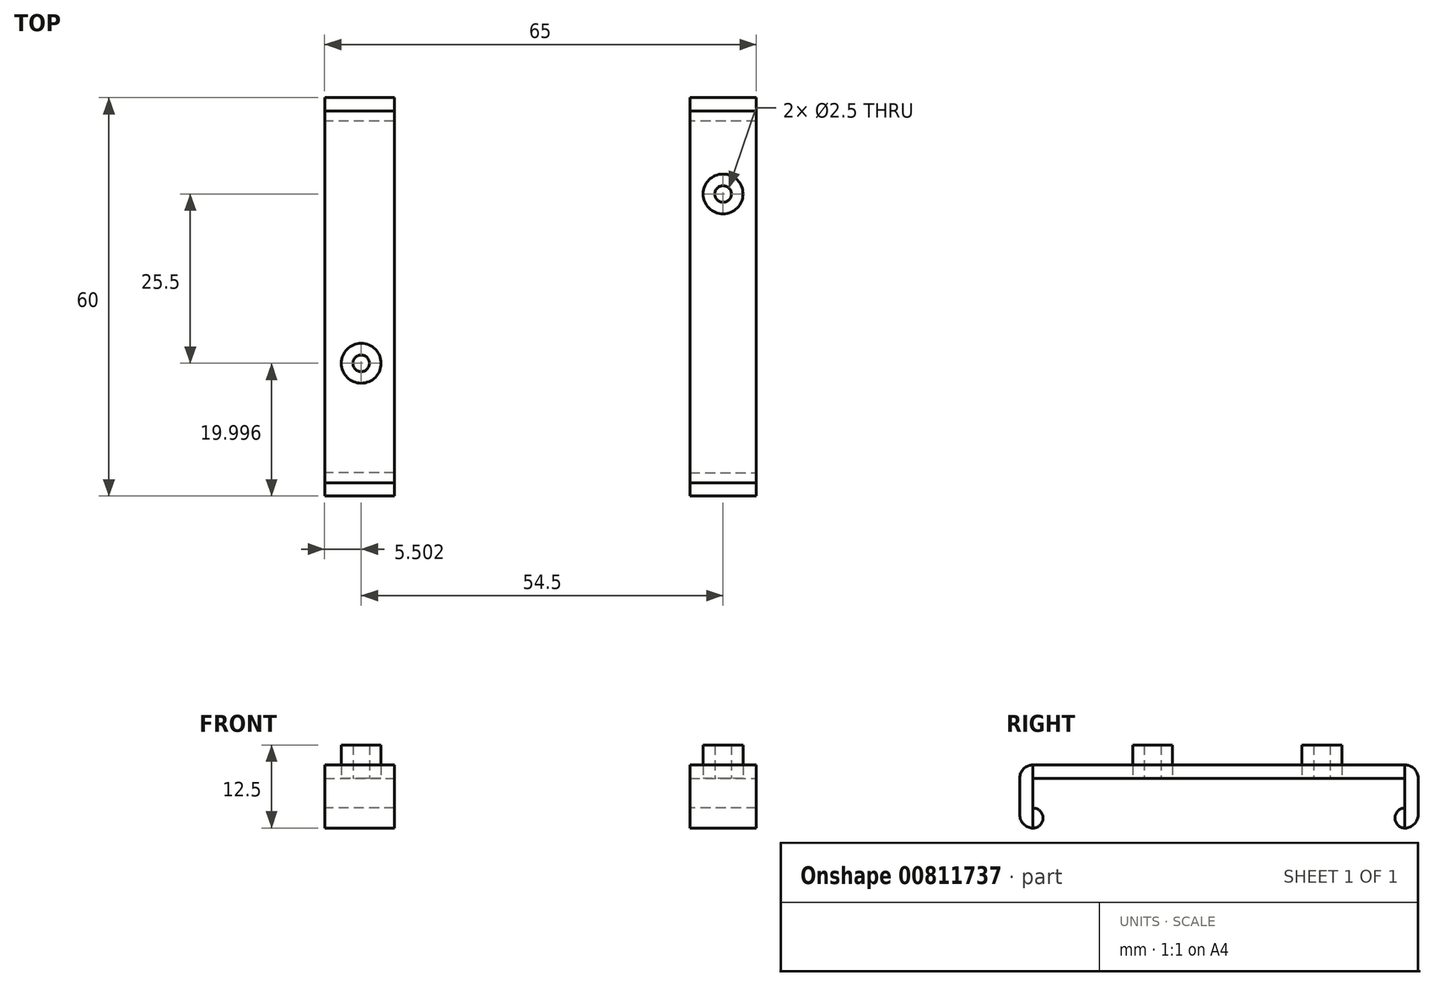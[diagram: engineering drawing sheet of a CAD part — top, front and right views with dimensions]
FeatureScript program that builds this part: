
annotation { "Feature Type Name" : "Feature", "Feature Type Description" : "" }
export const myFeature = defineFeature(function(context is Context, id is Id, definition is map)
    precondition{}
    {
        {
            var Q0;
            Q0=qCreatedBy(makeId("Top.planeOp"),FACE);
            var sketch = newSketch(context, id + "F0", { "sketchPlane" : qUnion([Q0])});
            skLineSegment(sketch, "E0.bottom", {"start": v(-22.77, 10.2) * mm, "end": v(62.23, 10.2) * mm, "construction": true});
            skLineSegment(sketch, "E0.top", {"start": v(-22.77, -45.8) * mm, "end": v(62.23, -45.8) * mm, "construction": true});
            skLineSegment(sketch, "E0.left", {"start": v(-22.77, 10.2) * mm, "end": v(-22.77, -45.8) * mm, "construction": true});
            skLineSegment(sketch, "E0.right", {"start": v(62.23, 10.2) * mm, "end": v(62.23, -45.8) * mm, "construction": true});
            skCircle(sketch, "E1", {"center": v(2.73, -27.8) * mm, "radius": 3 * mm});
            skCircle(sketch, "E2", {"center": v(2.73, -27.8) * mm, "radius": 1.25 * mm});
            skCircle(sketch, "E3", {"center": v(57.23, -2.3) * mm, "radius": 3 * mm});
            skCircle(sketch, "E4", {"center": v(57.23, -2.3) * mm, "radius": 1.25 * mm});
            skSolve(sketch);
        }
        {
            var Q0;
            Q0=makeQuery(id+"F0.imprint","IMPRINT",FACE,{"disambiguationData":[TD([[makeQuery(id+"F0.imprint","IMPRINT",EDGE,{"derivedFrom":sQuery(id+"F0.wireOp",EDGE,"E1")}),1.0]])]});
            var Q1;
            Q1=makeQuery(id+"F0.imprint","IMPRINT",FACE,{"disambiguationData":[TD([[makeQuery(id+"F0.imprint","IMPRINT",EDGE,{"derivedFrom":sQuery(id+"F0.wireOp",EDGE,"E3")}),1.0]])]});
            extrude(context, id + "F1", {"entities" : qUnion([Q0, Q1]), "depth" : 5 * mm, "offsetDistance" : 25 * mm});
        }
        {
            var Q0;
            Q0=qCreatedBy(makeId("Top.planeOp"),FACE);
            var sketch = newSketch(context, id + "F2", { "sketchPlane" : qUnion([Q0])});
            skLineSegment(sketch, "E5.bottom", {"start": v(-2.77, 10.2) * mm, "end": v(62.23, 10.2) * mm});
            skLineSegment(sketch, "E5.top", {"start": v(-2.77, -45.8) * mm, "end": v(62.23, -45.8) * mm});
            skLineSegment(sketch, "E5.left", {"start": v(-2.77, 10.2) * mm, "end": v(-2.77, -45.8) * mm});
            skLineSegment(sketch, "E5.right", {"start": v(62.23, 10.2) * mm, "end": v(62.23, -45.8) * mm});
            skLineSegment(sketch, "E6", {"start": v(7.73, 10.2) * mm, "end": v(7.73, -45.8) * mm});
            skLineSegment(sketch, "E7", {"start": v(52.23, 10.2) * mm, "end": v(52.23, -45.8) * mm});
            skSolve(sketch);
        }
        {
            var Q0;
            {var subQ0=sQuery(id+"F2.wireOp",EDGE,"E5.left");Q0=makeQuery(id+"F2.imprint","IMPRINT",FACE,{"disambiguationData":[TD([[makeQuery(id+"F2.imprint","IMPRINT",EDGE,{"derivedFrom":subQ0}),1.0]])]});}
            var Q1;
            {var subQ0=sQuery(id+"F2.wireOp",EDGE,"E5.right");Q1=makeQuery(id+"F2.imprint","IMPRINT",FACE,{"disambiguationData":[TD([[makeQuery(id+"F2.imprint","IMPRINT",EDGE,{"derivedFrom":subQ0}),-1.0]])]});}
            extrude(context, id + "F3", {"entities" : qUnion([Q0, Q1]), "depth" : 2 * mm, "offsetDistance" : 25 * mm});
        }
        {
            var Q0;
            Q0=makeQuery(id+"F3.opExtrude","SWEPT_FACE",FACE,{"disambiguationData":[OSD([sQuery(id+"F2.wireOp",EDGE,"E5.bottom")])]});
            var sketch = newSketch(context, id + "F4", { "sketchPlane" : qUnion([Q0])});
            skLineSegment(sketch, "E8.bottom", {"start": v(-62.23, 2) * mm, "end": v(-52.23, 2) * mm});
            skLineSegment(sketch, "E8.top", {"start": v(-62.23, -7.5) * mm, "end": v(-52.23, -7.5) * mm});
            skLineSegment(sketch, "E8.left", {"start": v(-62.23, 2) * mm, "end": v(-62.23, -7.5) * mm});
            skLineSegment(sketch, "E8.right", {"start": v(-52.23, 2) * mm, "end": v(-52.23, -7.5) * mm});
            skLineSegment(sketch, "E9", {"start": v(-62.23, -4.5) * mm, "end": v(-52.23, -4.5) * mm});
            skLineSegment(sketch, "E10.bottom", {"start": v(-7.73, 2) * mm, "end": v(2.77, 2) * mm});
            skLineSegment(sketch, "E10.top", {"start": v(-7.73, -7.5) * mm, "end": v(2.77, -7.5) * mm});
            skLineSegment(sketch, "E10.left", {"start": v(-7.73, 2) * mm, "end": v(-7.73, -7.5) * mm});
            skLineSegment(sketch, "E10.right", {"start": v(2.77, 2) * mm, "end": v(2.77, -7.5) * mm});
            skLineSegment(sketch, "E11", {"start": v(-7.73, -4.5) * mm, "end": v(2.77, -4.5) * mm});
            skSolve(sketch);
        }
        {
            var Q0;
            {var subQ0=sQuery(id+"F2.wireOp",EDGE,"E5.top");Q0=makeQuery(id+"F3.opExtrude","SWEPT_FACE",FACE,{"disambiguationData":[OSD([subQ0]),TDD([makeQuery(id+"F2.imprint","IMPRINT",EDGE,{"disambiguationData":[TD([[makeQuery(id+"F2.imprint","INTERSECT",VERTEX,{"derivedFrom":[subQ0,sQuery(id+"F2.wireOp",EDGE,"E5.left")]}),-1.0]])],"derivedFrom":subQ0})])]});}
            var sketch = newSketch(context, id + "F5", { "sketchPlane" : qUnion([Q0])});
            skLineSegment(sketch, "E12.bottom", {"start": v(-2.77, 2) * mm, "end": v(7.73, 2) * mm});
            skLineSegment(sketch, "E12.top", {"start": v(-2.77, -7.5) * mm, "end": v(7.73, -7.5) * mm});
            skLineSegment(sketch, "E12.left", {"start": v(-2.77, 2) * mm, "end": v(-2.77, -7.5) * mm});
            skLineSegment(sketch, "E12.right", {"start": v(7.73, 2) * mm, "end": v(7.73, -7.5) * mm});
            skLineSegment(sketch, "E13", {"start": v(-2.77, -4.5) * mm, "end": v(7.73, -4.5) * mm});
            skLineSegment(sketch, "E14.bottom", {"start": v(52.23, 2) * mm, "end": v(62.23, 2) * mm});
            skLineSegment(sketch, "E14.top", {"start": v(52.23, -7.5) * mm, "end": v(62.23, -7.5) * mm});
            skLineSegment(sketch, "E14.left", {"start": v(52.23, 2) * mm, "end": v(52.23, -7.5) * mm});
            skLineSegment(sketch, "E14.right", {"start": v(62.23, 2) * mm, "end": v(62.23, -7.5) * mm});
            skLineSegment(sketch, "E15", {"start": v(52.23, -4.5) * mm, "end": v(62.23, -4.5) * mm});
            skSolve(sketch);
        }
        {
            var Q0;
            {var subQ0=sQuery(id+"F4.wireOp",EDGE,"E10.bottom");Q0=makeQuery(id+"F4.imprint","IMPRINT",FACE,{"disambiguationData":[TD([[makeQuery(id+"F4.imprint","IMPRINT",EDGE,{"derivedFrom":subQ0}),1.0]])]});}
            var Q1;
            {var subQ3=sQuery(id+"F4.wireOp",EDGE,"E11");Q1=makeQuery(id+"F4.imprint","IMPRINT",FACE,{"disambiguationData":[TD([[makeQuery(id+"F4.imprint","IMPRINT",EDGE,{"derivedFrom":subQ3}),1.0]])]});}
            var Q2;
            {var subQ0=sQuery(id+"F4.wireOp",EDGE,"E10.top");Q2=makeQuery(id+"F4.imprint","IMPRINT",FACE,{"disambiguationData":[TD([[makeQuery(id+"F4.imprint","IMPRINT",EDGE,{"derivedFrom":subQ0}),1.0]])]});}
            var Q3;
            {var subQ0=sQuery(id+"F4.wireOp",EDGE,"E8.bottom");Q3=makeQuery(id+"F4.imprint","IMPRINT",FACE,{"disambiguationData":[TD([[makeQuery(id+"F4.imprint","IMPRINT",EDGE,{"derivedFrom":subQ0}),1.0]])]});}
            var Q4;
            {var subQ3=sQuery(id+"F4.wireOp",EDGE,"E9");Q4=makeQuery(id+"F4.imprint","IMPRINT",FACE,{"disambiguationData":[TD([[makeQuery(id+"F4.imprint","IMPRINT",EDGE,{"derivedFrom":subQ3}),1.0]])]});}
            var Q5;
            {var subQ0=sQuery(id+"F4.wireOp",EDGE,"E8.top");Q5=makeQuery(id+"F4.imprint","IMPRINT",FACE,{"disambiguationData":[TD([[makeQuery(id+"F4.imprint","IMPRINT",EDGE,{"derivedFrom":subQ0}),1.0]])]});}
            extrude(context, id + "F6", {"entities" : qUnion([Q0, Q1, Q2, Q3, Q4, Q5]), "depth" : 2 * mm, "offsetDistance" : 25 * mm});
        }
        {
            var Q0;
            {var subQ0=sQuery(id+"F5.wireOp",EDGE,"E12.bottom");Q0=makeQuery(id+"F5.imprint","IMPRINT",FACE,{"disambiguationData":[TD([[makeQuery(id+"F5.imprint","IMPRINT",EDGE,{"derivedFrom":subQ0}),-1.0]])]});}
            var Q1;
            {var subQ3=sQuery(id+"F5.wireOp",EDGE,"E13");Q1=makeQuery(id+"F5.imprint","IMPRINT",FACE,{"disambiguationData":[TD([[makeQuery(id+"F5.imprint","IMPRINT",EDGE,{"derivedFrom":subQ3}),1.0]])]});}
            var Q2;
            {var subQ0=sQuery(id+"F5.wireOp",EDGE,"E12.top");Q2=makeQuery(id+"F5.imprint","IMPRINT",FACE,{"disambiguationData":[TD([[makeQuery(id+"F5.imprint","IMPRINT",EDGE,{"derivedFrom":subQ0}),1.0]])]});}
            var Q3;
            {var subQ0=sQuery(id+"F5.wireOp",EDGE,"E14.bottom");Q3=makeQuery(id+"F5.imprint","IMPRINT",FACE,{"disambiguationData":[TD([[makeQuery(id+"F5.imprint","IMPRINT",EDGE,{"derivedFrom":subQ0}),-1.0]])]});}
            var Q4;
            {var subQ0=sQuery(id+"F5.wireOp",EDGE,"E14.top");Q4=makeQuery(id+"F5.imprint","IMPRINT",FACE,{"disambiguationData":[TD([[makeQuery(id+"F5.imprint","IMPRINT",EDGE,{"derivedFrom":subQ0}),1.0]])]});}
            extrude(context, id + "F7", {"entities" : qUnion([Q0, Q1, Q2, Q3, Q4]), "depth" : 2 * mm, "offsetDistance" : 25 * mm});
        }
        {
            var Q0;
            {var subQ0=sQuery(id+"F4.wireOp",EDGE,"E10.top");Q0=makeQuery(id+"F4.imprint","IMPRINT",FACE,{"disambiguationData":[TD([[makeQuery(id+"F4.imprint","IMPRINT",EDGE,{"derivedFrom":subQ0}),1.0]])]});}
            var Q1;
            {var subQ0=sQuery(id+"F4.wireOp",EDGE,"E8.top");Q1=makeQuery(id+"F4.imprint","IMPRINT",FACE,{"disambiguationData":[TD([[makeQuery(id+"F4.imprint","IMPRINT",EDGE,{"derivedFrom":subQ0}),1.0]])]});}
            extrude(context, id + "F8", {"entities" : qUnion([Q0, Q1]), "oppositeDirection" : true, "depth" : 1.5 * mm, "offsetDistance" : 25 * mm});
        }
        {
            var Q0;
            {var subQ0=sQuery(id+"F5.wireOp",EDGE,"E14.top");Q0=makeQuery(id+"F5.imprint","IMPRINT",FACE,{"disambiguationData":[TD([[makeQuery(id+"F5.imprint","IMPRINT",EDGE,{"derivedFrom":subQ0}),1.0]])]});}
            var Q1;
            {var subQ0=sQuery(id+"F5.wireOp",EDGE,"E12.top");Q1=makeQuery(id+"F5.imprint","IMPRINT",FACE,{"disambiguationData":[TD([[makeQuery(id+"F5.imprint","IMPRINT",EDGE,{"derivedFrom":subQ0}),1.0]])]});}
            extrude(context, id + "F9", {"entities" : qUnion([Q0, Q1]), "oppositeDirection" : true, "depth" : 1.5 * mm, "offsetDistance" : 25 * mm});
        }
        {
            var Q0;
            Q0=makeQuery(id+"F6.opExtrude","CAP_EDGE",EDGE,{"disambiguationData":[OSD([sQuery(id+"F4.wireOp",EDGE,"E8.bottom")])],"isStart":false});
            var Q1;
            Q1=makeQuery(id+"F7.opExtrude","CAP_EDGE",EDGE,{"disambiguationData":[OSD([sQuery(id+"F5.wireOp",EDGE,"E14.bottom")])],"isStart":false});
            var Q2;
            Q2=makeQuery(id+"F6.opExtrude","CAP_EDGE",EDGE,{"disambiguationData":[OSD([sQuery(id+"F4.wireOp",EDGE,"E10.bottom")])],"isStart":false});
            var Q3;
            Q3=makeQuery(id+"F7.opExtrude","CAP_EDGE",EDGE,{"disambiguationData":[OSD([sQuery(id+"F5.wireOp",EDGE,"E12.bottom")])],"isStart":false});
            var Q4;
            Q4=makeQuery(id+"F6.opExtrude","CAP_EDGE",EDGE,{"disambiguationData":[OSD([sQuery(id+"F4.wireOp",EDGE,"E10.top")])],"isStart":false});
            var Q5;
            Q5=makeQuery(id+"F6.opExtrude","CAP_EDGE",EDGE,{"disambiguationData":[OSD([sQuery(id+"F4.wireOp",EDGE,"E8.top")])],"isStart":false});
            var Q6;
            Q6=makeQuery(id+"F7.opExtrude","CAP_EDGE",EDGE,{"disambiguationData":[OSD([sQuery(id+"F5.wireOp",EDGE,"E14.top")])],"isStart":false});
            var Q7;
            Q7=makeQuery(id+"F7.opExtrude","CAP_EDGE",EDGE,{"disambiguationData":[OSD([sQuery(id+"F5.wireOp",EDGE,"E12.top")])],"isStart":false});
            fillet(context, id + "F10", {"entities" : qUnion([Q0, Q1, Q2, Q3, Q4, Q5, Q6, Q7]), "radius" : 2 * mm, "tangentPropagation" : true, "allowEdgeOverflow" : false});
        }
        {
            var Q0;
            Q0=makeQuery(id+"F9.opExtrude","CAP_EDGE",EDGE,{"disambiguationData":[OSD([sQuery(id+"F5.wireOp",EDGE,"E12.top")])],"isStart":false});
            var Q1;
            Q1=makeQuery(id+"F9.opExtrude","CAP_EDGE",EDGE,{"disambiguationData":[OSD([sQuery(id+"F5.wireOp",EDGE,"E13")])],"isStart":false});
            var Q2;
            Q2=makeQuery(id+"F9.opExtrude","CAP_EDGE",EDGE,{"disambiguationData":[OSD([sQuery(id+"F5.wireOp",EDGE,"E15")])],"isStart":false});
            var Q3;
            Q3=makeQuery(id+"F9.opExtrude","CAP_EDGE",EDGE,{"disambiguationData":[OSD([sQuery(id+"F5.wireOp",EDGE,"E14.top")])],"isStart":false});
            var Q4;
            Q4=makeQuery(id+"F8.opExtrude","CAP_EDGE",EDGE,{"disambiguationData":[OSD([sQuery(id+"F4.wireOp",EDGE,"E9")])],"isStart":false});
            var Q5;
            Q5=makeQuery(id+"F8.opExtrude","CAP_EDGE",EDGE,{"disambiguationData":[OSD([sQuery(id+"F4.wireOp",EDGE,"E11")])],"isStart":false});
            var Q6;
            Q6=makeQuery(id+"F8.opExtrude","CAP_EDGE",EDGE,{"disambiguationData":[OSD([sQuery(id+"F4.wireOp",EDGE,"E10.top")])],"isStart":false});
            var Q7;
            Q7=makeQuery(id+"F8.opExtrude","CAP_EDGE",EDGE,{"disambiguationData":[OSD([sQuery(id+"F4.wireOp",EDGE,"E8.top")])],"isStart":false});
            fillet(context, id + "F11", {"entities" : qUnion([Q0, Q1, Q2, Q3, Q4, Q5, Q6, Q7]), "radius" : 1.5 * mm, "tangentPropagation" : true, "allowEdgeOverflow" : false});
        }
    });
